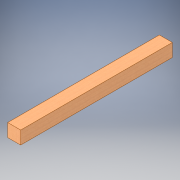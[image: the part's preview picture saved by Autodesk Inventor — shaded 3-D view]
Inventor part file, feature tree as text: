
AUTODESK INVENTOR PART (.ipt)
format: ipt  version: 2019 (Build 230136000, 136)  size: 113,664 bytes
history: native  units: mm
features: other x3, extrude x1, sketch x1
ambient origin geometry x8: Origin, YZ Plane, XZ Plane, XY Plane, X Axis, Y Axis, Z Axis, Center Point
bodies: Body1 (feature_tree)
feature tree (5):
  other  "Таблица"
  other  "Столб-01"
  other  "Твердое тело1"
  extrude  "Выдавливание1"  TaperAngle=0.0deg  [1 undecoded]
  sketch  "Эскиз1"
note: 1 required parameter value undecoded (feature->parameter linkage not recoverable at this tier; creation-order binding heuristic only, values carry confidence <= 0.55)
